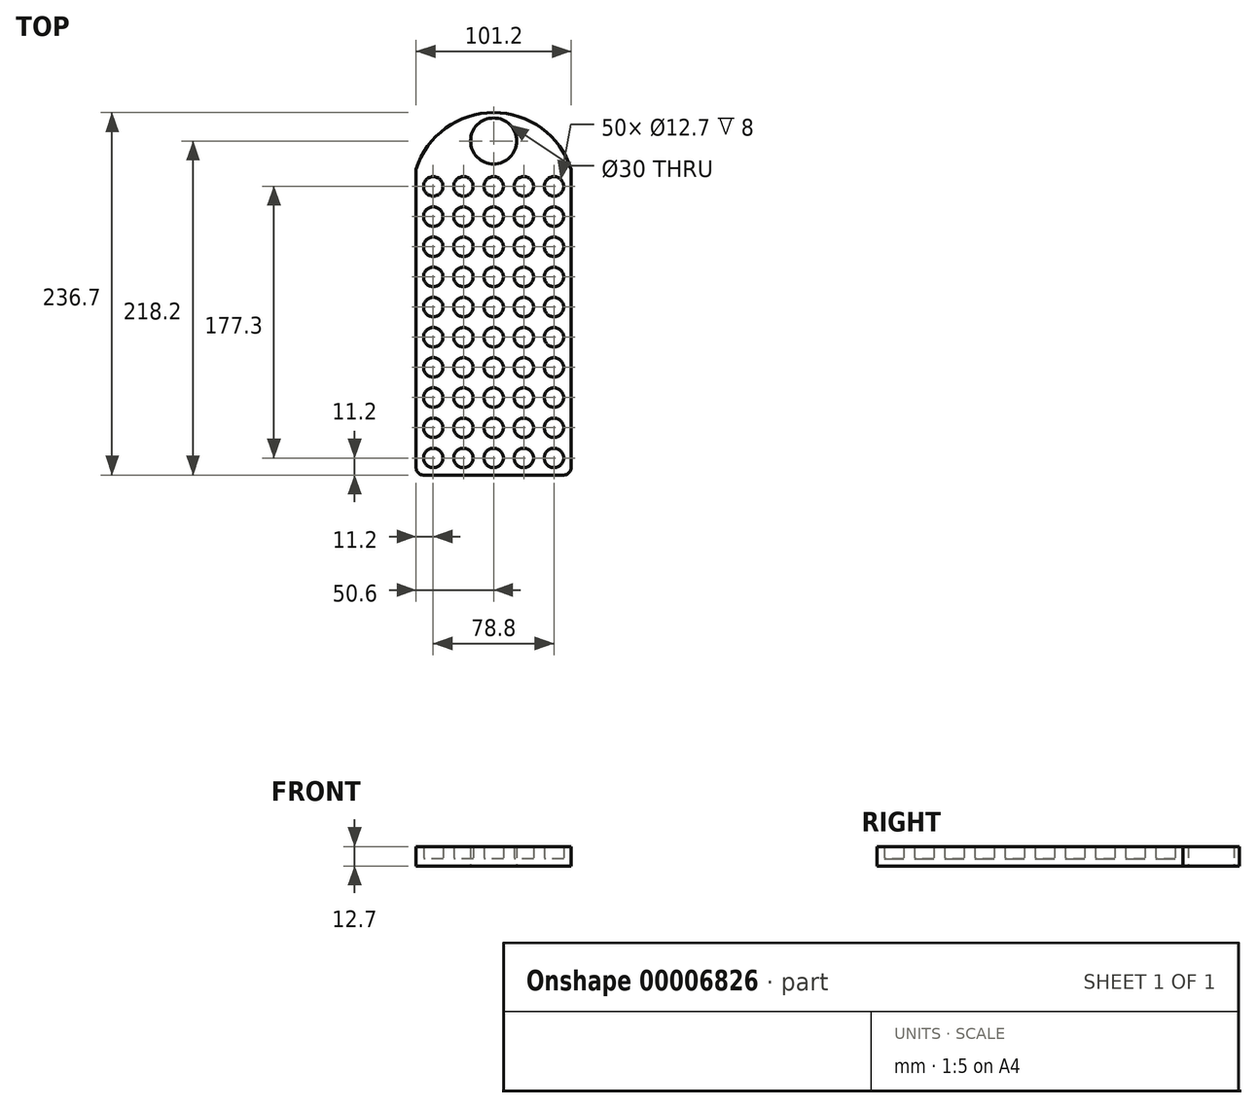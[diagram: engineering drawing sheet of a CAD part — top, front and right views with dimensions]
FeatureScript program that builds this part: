
annotation { "Feature Type Name" : "Feature", "Feature Type Description" : "" }
export const myFeature = defineFeature(function(context is Context, id is Id, definition is map)
    precondition{}
    {
        {
            var Q0;
            Q0=qCreatedBy(makeId("Top.planeOp"),FACE);
            var sketch = newSketch(context, id + "F0", { "sketchPlane" : qUnion([Q0])});
            skLineSegment(sketch, "E0", {"start": v(0, 0) * mm, "end": v(11.2, 0) * mm, "construction": true});
            skLineSegment(sketch, "E1", {"start": v(11.2, 0) * mm, "end": v(30.9, 0) * mm, "construction": true});
            skLineSegment(sketch, "E2", {"start": v(25.5, 0) * mm, "end": v(30.9, 0) * mm, "construction": true});
            skLineSegment(sketch, "E3", {"start": v(47.9, 0) * mm, "end": v(50.6, 0) * mm, "construction": true});
            skLineSegment(sketch, "E4", {"start": v(0, 0) * mm, "end": v(0, 11.2) * mm, "construction": true});
            skLineSegment(sketch, "E5", {"start": v(0, 11.2) * mm, "end": v(70.3, 11.2) * mm, "construction": true});
            skLineSegment(sketch, "E6", {"start": v(11.2, 0) * mm, "end": v(11.2, 11.2) * mm, "construction": true});
            skLineSegment(sketch, "E7", {"start": v(30.9, 0) * mm, "end": v(30.9, 11.2) * mm, "construction": true});
            skLineSegment(sketch, "E8", {"start": v(50.6, 0) * mm, "end": v(50.6, 11.2) * mm, "construction": true});
            skLineSegment(sketch, "E9", {"start": v(70.3, 0) * mm, "end": v(70.3, 11.2) * mm, "construction": true});
            skCircle(sketch, "E10", {"center": v(11.2, 11.2) * mm, "radius": 6.35 * mm});
            skLineSegment(sketch, "E11", {"start": v(70.3, 0) * mm, "end": v(90, 0) * mm, "construction": true});
            skLineSegment(sketch, "E12", {"start": v(70.3, 11.2) * mm, "end": v(90, 11.2) * mm, "construction": true});
            skLineSegment(sketch, "E13", {"start": v(90, 0) * mm, "end": v(90, 11.2) * mm, "construction": true});
            skCircle(sketch, "E14", {"center": v(30.9, 11.2) * mm, "radius": 6.35 * mm});
            skCircle(sketch, "E15", {"center": v(50.6, 11.2) * mm, "radius": 6.35 * mm});
            skCircle(sketch, "E16", {"center": v(70.3, 11.2) * mm, "radius": 6.35 * mm});
            skLineSegment(sketch, "E17", {"start": v(90, 0) * mm, "end": v(101.2, 0) * mm, "construction": true});
            skLineSegment(sketch, "E18", {"start": v(101.2, 11.2) * mm, "end": v(90, 11.2) * mm, "construction": true});
            skLineSegment(sketch, "E19", {"start": v(101.2, 0) * mm, "end": v(101.2, 11.2) * mm});
            skCircle(sketch, "E20", {"center": v(90, 11.2) * mm, "radius": 6.35 * mm});
            skLineSegment(sketch, "E21", {"start": v(0, 11.2) * mm, "end": v(0, 30.9) * mm, "construction": true});
            skLineSegment(sketch, "E22", {"start": v(0, 30.9) * mm, "end": v(101.2, 30.9) * mm, "construction": true});
            skLineSegment(sketch, "E23", {"start": v(11.2, 11.2) * mm, "end": v(11.2, 30.9) * mm, "construction": true});
            skLineSegment(sketch, "E24", {"start": v(30.9, 11.2) * mm, "end": v(30.9, 30.9) * mm, "construction": true});
            skLineSegment(sketch, "E25", {"start": v(50.6, 11.2) * mm, "end": v(50.6, 30.9) * mm, "construction": true});
            skLineSegment(sketch, "E26", {"start": v(70.3, 11.2) * mm, "end": v(70.3, 30.9) * mm, "construction": true});
            skLineSegment(sketch, "E27", {"start": v(90, 11.2) * mm, "end": v(90, 30.9) * mm, "construction": true});
            skLineSegment(sketch, "E28", {"start": v(101.2, 11.2) * mm, "end": v(101.2, 30.9) * mm, "construction": true});
            skCircle(sketch, "E29", {"center": v(11.2, 30.9) * mm, "radius": 6.35 * mm});
            skCircle(sketch, "E30", {"center": v(30.9, 30.9) * mm, "radius": 6.35 * mm});
            skCircle(sketch, "E31", {"center": v(50.6, 30.9) * mm, "radius": 6.35 * mm});
            skCircle(sketch, "E32", {"center": v(70.3, 30.9) * mm, "radius": 6.35 * mm});
            skCircle(sketch, "E33", {"center": v(90, 30.9) * mm, "radius": 6.35 * mm});
            skLineSegment(sketch, "E34", {"start": v(0, 30.9) * mm, "end": v(0, 50.6) * mm, "construction": true});
            skLineSegment(sketch, "E35", {"start": v(0, 50.6) * mm, "end": v(101.2, 50.6) * mm, "construction": true});
            skLineSegment(sketch, "E36", {"start": v(101.2, 30.9) * mm, "end": v(101.2, 50.6) * mm, "construction": true});
            skLineSegment(sketch, "E37", {"start": v(90, 30.9) * mm, "end": v(90, 50.6) * mm, "construction": true});
            skLineSegment(sketch, "E38", {"start": v(70.3, 30.9) * mm, "end": v(70.3, 50.6) * mm, "construction": true});
            skLineSegment(sketch, "E39", {"start": v(50.6, 30.9) * mm, "end": v(50.6, 50.6) * mm, "construction": true});
            skLineSegment(sketch, "E40", {"start": v(30.9, 30.9) * mm, "end": v(30.9, 50.6) * mm, "construction": true});
            skLineSegment(sketch, "E41", {"start": v(11.2, 30.9) * mm, "end": v(11.2, 50.6) * mm, "construction": true});
            skLineSegment(sketch, "E42", {"start": v(0, 50.6) * mm, "end": v(0, 70.3) * mm, "construction": true});
            skLineSegment(sketch, "E43", {"start": v(0, 70.3) * mm, "end": v(101.2, 70.3) * mm, "construction": true});
            skLineSegment(sketch, "E44", {"start": v(101.2, 50.6) * mm, "end": v(101.2, 70.3) * mm, "construction": true});
            skLineSegment(sketch, "E45", {"start": v(90, 50.6) * mm, "end": v(90, 70.3) * mm, "construction": true});
            skLineSegment(sketch, "E46", {"start": v(70.3, 50.6) * mm, "end": v(70.3, 70.3) * mm, "construction": true});
            skLineSegment(sketch, "E47", {"start": v(50.6, 50.6) * mm, "end": v(50.6, 70.3) * mm, "construction": true});
            skLineSegment(sketch, "E48", {"start": v(30.9, 50.6) * mm, "end": v(30.9, 70.3) * mm, "construction": true});
            skLineSegment(sketch, "E49", {"start": v(11.2, 50.6) * mm, "end": v(11.2, 70.3) * mm, "construction": true});
            skLineSegment(sketch, "E50", {"start": v(0, 70.3) * mm, "end": v(0, 90) * mm, "construction": true});
            skLineSegment(sketch, "E51", {"start": v(0, 90) * mm, "end": v(84.97, 90) * mm, "construction": true});
            skLineSegment(sketch, "E52", {"start": v(11.2, 70.3) * mm, "end": v(11.2, 90) * mm, "construction": true});
            skLineSegment(sketch, "E53", {"start": v(30.9, 70.3) * mm, "end": v(30.9, 90) * mm, "construction": true});
            skLineSegment(sketch, "E54", {"start": v(50.6, 70.3) * mm, "end": v(50.6, 90) * mm, "construction": true});
            skLineSegment(sketch, "E55", {"start": v(70.3, 70.3) * mm, "end": v(70.3, 90) * mm, "construction": true});
            skLineSegment(sketch, "E56", {"start": v(90, 70.3) * mm, "end": v(90, 90) * mm, "construction": true});
            skLineSegment(sketch, "E57", {"start": v(101.2, 70.3) * mm, "end": v(101.2, 90) * mm, "construction": true});
            skCircle(sketch, "E58", {"center": v(11.2, 50.6) * mm, "radius": 6.35 * mm});
            skCircle(sketch, "E59", {"center": v(11.2, 70.3) * mm, "radius": 6.35 * mm});
            skCircle(sketch, "E60", {"center": v(11.2, 90) * mm, "radius": 6.35 * mm});
            skCircle(sketch, "E61", {"center": v(30.9, 90) * mm, "radius": 6.35 * mm});
            skCircle(sketch, "E62", {"center": v(30.9, 70.3) * mm, "radius": 6.35 * mm});
            skCircle(sketch, "E63", {"center": v(30.9, 50.6) * mm, "radius": 6.35 * mm});
            skCircle(sketch, "E64", {"center": v(50.6, 90) * mm, "radius": 6.35 * mm});
            skCircle(sketch, "E65", {"center": v(50.6, 70.3) * mm, "radius": 6.35 * mm});
            skCircle(sketch, "E66", {"center": v(50.6, 50.6) * mm, "radius": 6.35 * mm});
            skCircle(sketch, "E67", {"center": v(70.3, 50.6) * mm, "radius": 6.35 * mm});
            skCircle(sketch, "E68", {"center": v(70.3, 70.3) * mm, "radius": 6.35 * mm});
            skCircle(sketch, "E69", {"center": v(70.3, 90) * mm, "radius": 6.35 * mm});
            skCircle(sketch, "E70", {"center": v(90, 90) * mm, "radius": 6.35 * mm});
            skCircle(sketch, "E71", {"center": v(90, 70.3) * mm, "radius": 6.35 * mm});
            skCircle(sketch, "E72", {"center": v(90, 50.6) * mm, "radius": 6.35 * mm});
            skLineSegment(sketch, "E73", {"start": v(0, 90) * mm, "end": v(0, 109.7) * mm, "construction": true});
            skLineSegment(sketch, "E74", {"start": v(0, 109.7) * mm, "end": v(101.2, 109.7) * mm, "construction": true});
            skLineSegment(sketch, "E75", {"start": v(11.2, 90) * mm, "end": v(11.2, 109.7) * mm, "construction": true});
            skLineSegment(sketch, "E76", {"start": v(30.9, 90) * mm, "end": v(30.9, 109.7) * mm, "construction": true});
            skLineSegment(sketch, "E77", {"start": v(50.6, 90) * mm, "end": v(50.6, 109.7) * mm, "construction": true});
            skLineSegment(sketch, "E78", {"start": v(70.3, 90) * mm, "end": v(70.3, 109.7) * mm, "construction": true});
            skLineSegment(sketch, "E79", {"start": v(89.88, 87.08) * mm, "end": v(90, 109.7) * mm, "construction": true});
            skLineSegment(sketch, "E80", {"start": v(90, 109.7) * mm, "end": v(90, 109.7) * mm});
            skLineSegment(sketch, "E81", {"start": v(101.2, 90) * mm, "end": v(101.2, 109.7) * mm, "construction": true});
            skLineSegment(sketch, "E82", {"start": v(0, 109.7) * mm, "end": v(0, 129.4) * mm, "construction": true});
            skLineSegment(sketch, "E83", {"start": v(0, 129.4) * mm, "end": v(101.2, 129.4) * mm, "construction": true});
            skLineSegment(sketch, "E84", {"start": v(11.2, 109.7) * mm, "end": v(11.2, 129.4) * mm, "construction": true});
            skLineSegment(sketch, "E85", {"start": v(30.9, 109.7) * mm, "end": v(30.9, 129.4) * mm, "construction": true});
            skLineSegment(sketch, "E86", {"start": v(50.6, 109.7) * mm, "end": v(50.6, 129.4) * mm, "construction": true});
            skLineSegment(sketch, "E87", {"start": v(70.3, 109.7) * mm, "end": v(70.3, 129.4) * mm, "construction": true});
            skLineSegment(sketch, "E88", {"start": v(90, 109.7) * mm, "end": v(90, 129.4) * mm, "construction": true});
            skLineSegment(sketch, "E89", {"start": v(101.2, 109.7) * mm, "end": v(101.2, 129.4) * mm, "construction": true});
            skLineSegment(sketch, "E90", {"start": v(0, 129.4) * mm, "end": v(0, 149.1) * mm, "construction": true});
            skLineSegment(sketch, "E91", {"start": v(0, 149.1) * mm, "end": v(101.2, 149.1) * mm, "construction": true});
            skLineSegment(sketch, "E92", {"start": v(11.2, 129.4) * mm, "end": v(11.2, 149.1) * mm, "construction": true});
            skLineSegment(sketch, "E93", {"start": v(30.9, 129.4) * mm, "end": v(30.9, 149.1) * mm, "construction": true});
            skLineSegment(sketch, "E94", {"start": v(50.6, 129.4) * mm, "end": v(50.6, 149.1) * mm, "construction": true});
            skLineSegment(sketch, "E95", {"start": v(70.3, 129.4) * mm, "end": v(70.3, 149.1) * mm, "construction": true});
            skLineSegment(sketch, "E96", {"start": v(90, 129.4) * mm, "end": v(90, 149.1) * mm, "construction": true});
            skLineSegment(sketch, "E97", {"start": v(101.2, 129.4) * mm, "end": v(101.2, 149.1) * mm, "construction": true});
            skLineSegment(sketch, "E98", {"start": v(0, 149.1) * mm, "end": v(0, 168.8) * mm, "construction": true});
            skLineSegment(sketch, "E99", {"start": v(0, 168.8) * mm, "end": v(101.2, 168.8) * mm, "construction": true});
            skLineSegment(sketch, "E100", {"start": v(11.2, 149.1) * mm, "end": v(11.2, 168.8) * mm, "construction": true});
            skLineSegment(sketch, "E101", {"start": v(30.9, 149.1) * mm, "end": v(30.9, 168.8) * mm, "construction": true});
            skLineSegment(sketch, "E102", {"start": v(50.6, 149.1) * mm, "end": v(50.6, 168.8) * mm, "construction": true});
            skLineSegment(sketch, "E103", {"start": v(70.3, 149.1) * mm, "end": v(70.3, 168.8) * mm, "construction": true});
            skLineSegment(sketch, "E104", {"start": v(90, 149.1) * mm, "end": v(90, 168.8) * mm, "construction": true});
            skLineSegment(sketch, "E105", {"start": v(101.2, 149.1) * mm, "end": v(101.2, 168.8) * mm, "construction": true});
            skLineSegment(sketch, "E106", {"start": v(0, 168.8) * mm, "end": v(0, 188.5) * mm, "construction": true});
            skLineSegment(sketch, "E107", {"start": v(0, 188.5) * mm, "end": v(101.2, 188.5) * mm, "construction": true});
            skLineSegment(sketch, "E108", {"start": v(11.2, 168.8) * mm, "end": v(11.2, 188.5) * mm, "construction": true});
            skLineSegment(sketch, "E109", {"start": v(30.9, 168.8) * mm, "end": v(30.9, 188.5) * mm, "construction": true});
            skLineSegment(sketch, "E110", {"start": v(50.6, 168.8) * mm, "end": v(50.6, 188.5) * mm, "construction": true});
            skLineSegment(sketch, "E111", {"start": v(70.3, 168.8) * mm, "end": v(70.3, 188.5) * mm, "construction": true});
            skLineSegment(sketch, "E112", {"start": v(90, 168.8) * mm, "end": v(90, 188.5) * mm, "construction": true});
            skLineSegment(sketch, "E113", {"start": v(101.2, 168.8) * mm, "end": v(101.2, 188.5) * mm, "construction": true});
            skCircle(sketch, "E114", {"center": v(11.2, 188.5) * mm, "radius": 6.35 * mm});
            skCircle(sketch, "E115", {"center": v(11.2, 168.8) * mm, "radius": 6.35 * mm});
            skCircle(sketch, "E116", {"center": v(11.2, 149.1) * mm, "radius": 6.35 * mm});
            skCircle(sketch, "E117", {"center": v(11.2, 129.4) * mm, "radius": 6.35 * mm});
            skCircle(sketch, "E118", {"center": v(11.2, 109.7) * mm, "radius": 6.35 * mm});
            skCircle(sketch, "E119", {"center": v(30.9, 109.7) * mm, "radius": 6.35 * mm});
            skCircle(sketch, "E120", {"center": v(30.9, 129.4) * mm, "radius": 6.35 * mm});
            skCircle(sketch, "E121", {"center": v(30.9, 149.1) * mm, "radius": 6.35 * mm});
            skCircle(sketch, "E122", {"center": v(30.9, 168.8) * mm, "radius": 6.35 * mm});
            skCircle(sketch, "E123", {"center": v(30.9, 188.5) * mm, "radius": 6.35 * mm});
            skCircle(sketch, "E124", {"center": v(50.6, 188.5) * mm, "radius": 6.35 * mm});
            skCircle(sketch, "E125", {"center": v(50.6, 168.8) * mm, "radius": 6.35 * mm});
            skCircle(sketch, "E126", {"center": v(50.6, 149.1) * mm, "radius": 6.35 * mm});
            skCircle(sketch, "E127", {"center": v(50.6, 129.4) * mm, "radius": 6.35 * mm});
            skCircle(sketch, "E128", {"center": v(50.6, 109.7) * mm, "radius": 6.35 * mm});
            skCircle(sketch, "E129", {"center": v(90, 109.7) * mm, "radius": 6.35 * mm});
            skCircle(sketch, "E130", {"center": v(70.3, 109.7) * mm, "radius": 6.35 * mm});
            skCircle(sketch, "E131", {"center": v(70.3, 129.4) * mm, "radius": 6.35 * mm});
            skCircle(sketch, "E132", {"center": v(90, 129.4) * mm, "radius": 6.35 * mm});
            skCircle(sketch, "E133", {"center": v(90, 149.1) * mm, "radius": 6.35 * mm});
            skCircle(sketch, "E134", {"center": v(70.3, 149.1) * mm, "radius": 6.35 * mm});
            skCircle(sketch, "E135", {"center": v(70.3, 168.8) * mm, "radius": 6.35 * mm});
            skCircle(sketch, "E136", {"center": v(90, 168.8) * mm, "radius": 6.35 * mm});
            skCircle(sketch, "E137", {"center": v(70.3, 188.5) * mm, "radius": 6.35 * mm});
            skCircle(sketch, "E138", {"center": v(90, 188.5) * mm, "radius": 6.35 * mm});
            skLineSegment(sketch, "E139", {"start": v(101.2, 188.5) * mm, "end": v(101.2, 199.7) * mm, "construction": true});
            skLineSegment(sketch, "E140", {"start": v(30.9, 0) * mm, "end": v(50.6, 0) * mm, "construction": true});
            skLineSegment(sketch, "E141", {"start": v(50.6, 0) * mm, "end": v(70.3, 0) * mm, "construction": true});
            skSolve(sketch);
        }
        {
            var Q0;
            Q0=qCreatedBy(makeId("Top.planeOp"),FACE);
            var sketch = newSketch(context, id + "F1", { "sketchPlane" : qUnion([Q0])});
            skLineSegment(sketch, "E142.bottom", {"start": v(5, 0) * mm, "end": v(96.2, 0) * mm});
            skLineSegment(sketch, "E142.top", {"start": v(0, 199.7) * mm, "end": v(101.2, 199.7) * mm, "construction": true});
            skLineSegment(sketch, "E142.left", {"start": v(0, 5) * mm, "end": v(0, 199.7) * mm});
            skLineSegment(sketch, "E142.right", {"start": v(101.2, 5) * mm, "end": v(101.2, 199.7) * mm});
            skPoint(sketch, "E143.visualSharp", {"position": v(101.2, 0) * mm});
            skArc(sketch, "E143.filletArc", {"start": v(96.2, 0) * mm, "mid": v(99.74, 1.46) * mm, "end": v(101.2, 5) * mm});
            skPoint(sketch, "E144.visualSharp", {"position": v(0, 0) * mm});
            skArc(sketch, "E144.filletArc", {"start": v(0, 5) * mm, "mid": v(1.46, 1.46) * mm, "end": v(5, 0) * mm});
            skLineSegment(sketch, "E145", {"start": v(50.6, 199.7) * mm, "end": v(50.6, 218.2) * mm, "construction": true});
            skCircle(sketch, "E146", {"center": v(50.6, 218.2) * mm, "radius": 15 * mm});
            skLineSegment(sketch, "E147", {"start": v(50.6, 218.2) * mm, "end": v(50.6, 233.2) * mm, "construction": true});
            skLineSegment(sketch, "E148", {"start": v(50.6, 233.2) * mm, "end": v(50.6, 236.7) * mm, "construction": true});
            skLineSegment(sketch, "E149", {"start": v(50.6, 199.7) * mm, "end": v(50.6, 203.2) * mm, "construction": true});
            skArc(sketch, "E150", {"start": v(101.2, 199.7) * mm, "mid": v(50.6, 236.7) * mm, "end": v(0, 199.7) * mm});
            skSolve(sketch);
        }
        {
            var Q0;
            Q0=qSketchRegion(id+"F0",true);
            extrude(context, id + "F2", {"entities" : qUnion([Q0]), "depth" : 4.7 * mm});
        }
        {
            var Q0;
            Q0=makeQuery(id+"F2.opExtrude","CAP_FACE",FACE,{"disambiguationData":[OSD([sQuery(id+"F0.wireOp",EDGE,"E15")])],"isStart":false});
            var Q1;
            Q1=makeQuery(id+"F2.opExtrude","CAP_FACE",FACE,{"disambiguationData":[OSD([sQuery(id+"F0.wireOp",EDGE,"E16")])],"isStart":false});
            var Q2;
            Q2=makeQuery(id+"F2.opExtrude","CAP_FACE",FACE,{"disambiguationData":[OSD([sQuery(id+"F0.wireOp",EDGE,"E20")])],"isStart":false});
            var Q3;
            Q3=makeQuery(id+"F2.opExtrude","CAP_FACE",FACE,{"disambiguationData":[OSD([sQuery(id+"F0.wireOp",EDGE,"E33")])],"isStart":false});
            var Q4;
            Q4=makeQuery(id+"F2.opExtrude","CAP_FACE",FACE,{"disambiguationData":[OSD([sQuery(id+"F0.wireOp",EDGE,"E32")])],"isStart":false});
            var Q5;
            Q5=makeQuery(id+"F2.opExtrude","CAP_FACE",FACE,{"disambiguationData":[OSD([sQuery(id+"F0.wireOp",EDGE,"E31")])],"isStart":false});
            var Q6;
            Q6=makeQuery(id+"F2.opExtrude","CAP_FACE",FACE,{"disambiguationData":[OSD([sQuery(id+"F0.wireOp",EDGE,"E30")])],"isStart":false});
            var Q7;
            Q7=makeQuery(id+"F2.opExtrude","CAP_FACE",FACE,{"disambiguationData":[OSD([sQuery(id+"F0.wireOp",EDGE,"E14")])],"isStart":false});
            var Q8;
            Q8=makeQuery(id+"F2.opExtrude","CAP_FACE",FACE,{"disambiguationData":[OSD([sQuery(id+"F0.wireOp",EDGE,"E10")])],"isStart":false});
            var Q9;
            Q9=makeQuery(id+"F2.opExtrude","CAP_FACE",FACE,{"disambiguationData":[OSD([sQuery(id+"F0.wireOp",EDGE,"E29")])],"isStart":false});
            var Q10;
            Q10=makeQuery(id+"F2.opExtrude","CAP_FACE",FACE,{"disambiguationData":[OSD([sQuery(id+"F0.wireOp",EDGE,"E58")])],"isStart":false});
            var Q11;
            Q11=makeQuery(id+"F2.opExtrude","CAP_FACE",FACE,{"disambiguationData":[OSD([sQuery(id+"F0.wireOp",EDGE,"E63")])],"isStart":false});
            var Q12;
            Q12=makeQuery(id+"F2.opExtrude","CAP_FACE",FACE,{"disambiguationData":[OSD([sQuery(id+"F0.wireOp",EDGE,"E66")])],"isStart":false});
            var Q13;
            Q13=makeQuery(id+"F2.opExtrude","CAP_FACE",FACE,{"disambiguationData":[OSD([sQuery(id+"F0.wireOp",EDGE,"E67")])],"isStart":false});
            var Q14;
            Q14=makeQuery(id+"F2.opExtrude","CAP_FACE",FACE,{"disambiguationData":[OSD([sQuery(id+"F0.wireOp",EDGE,"E72")])],"isStart":false});
            var Q15;
            Q15=makeQuery(id+"F2.opExtrude","CAP_FACE",FACE,{"disambiguationData":[OSD([sQuery(id+"F0.wireOp",EDGE,"E71")])],"isStart":false});
            var Q16;
            Q16=makeQuery(id+"F2.opExtrude","CAP_FACE",FACE,{"disambiguationData":[OSD([sQuery(id+"F0.wireOp",EDGE,"E68")])],"isStart":false});
            var Q17;
            Q17=makeQuery(id+"F2.opExtrude","CAP_FACE",FACE,{"disambiguationData":[OSD([sQuery(id+"F0.wireOp",EDGE,"E65")])],"isStart":false});
            var Q18;
            Q18=makeQuery(id+"F2.opExtrude","CAP_FACE",FACE,{"disambiguationData":[OSD([sQuery(id+"F0.wireOp",EDGE,"E62")])],"isStart":false});
            var Q19;
            Q19=makeQuery(id+"F2.opExtrude","CAP_FACE",FACE,{"disambiguationData":[OSD([sQuery(id+"F0.wireOp",EDGE,"E59")])],"isStart":false});
            var Q20;
            Q20=makeQuery(id+"F2.opExtrude","CAP_FACE",FACE,{"disambiguationData":[OSD([sQuery(id+"F0.wireOp",EDGE,"E60")])],"isStart":false});
            var Q21;
            Q21=makeQuery(id+"F2.opExtrude","CAP_FACE",FACE,{"disambiguationData":[OSD([sQuery(id+"F0.wireOp",EDGE,"E118")])],"isStart":false});
            var Q22;
            Q22=makeQuery(id+"F2.opExtrude","CAP_FACE",FACE,{"disambiguationData":[OSD([sQuery(id+"F0.wireOp",EDGE,"E117")])],"isStart":false});
            var Q23;
            Q23=makeQuery(id+"F2.opExtrude","CAP_FACE",FACE,{"disambiguationData":[OSD([sQuery(id+"F0.wireOp",EDGE,"E116")])],"isStart":false});
            var Q24;
            Q24=makeQuery(id+"F2.opExtrude","CAP_FACE",FACE,{"disambiguationData":[OSD([sQuery(id+"F0.wireOp",EDGE,"E115")])],"isStart":false});
            var Q25;
            Q25=makeQuery(id+"F2.opExtrude","CAP_FACE",FACE,{"disambiguationData":[OSD([sQuery(id+"F0.wireOp",EDGE,"E114")])],"isStart":false});
            var Q26;
            Q26=makeQuery(id+"F2.opExtrude","CAP_FACE",FACE,{"disambiguationData":[OSD([sQuery(id+"F0.wireOp",EDGE,"E123")])],"isStart":false});
            var Q27;
            Q27=makeQuery(id+"F2.opExtrude","CAP_FACE",FACE,{"disambiguationData":[OSD([sQuery(id+"F0.wireOp",EDGE,"E122")])],"isStart":false});
            var Q28;
            Q28=makeQuery(id+"F2.opExtrude","CAP_FACE",FACE,{"disambiguationData":[OSD([sQuery(id+"F0.wireOp",EDGE,"E121")])],"isStart":false});
            var Q29;
            Q29=makeQuery(id+"F2.opExtrude","CAP_FACE",FACE,{"disambiguationData":[OSD([sQuery(id+"F0.wireOp",EDGE,"E120")])],"isStart":false});
            var Q30;
            Q30=makeQuery(id+"F2.opExtrude","CAP_FACE",FACE,{"disambiguationData":[OSD([sQuery(id+"F0.wireOp",EDGE,"E119")])],"isStart":false});
            var Q31;
            Q31=makeQuery(id+"F2.opExtrude","CAP_FACE",FACE,{"disambiguationData":[OSD([sQuery(id+"F0.wireOp",EDGE,"E61")])],"isStart":false});
            var Q32;
            Q32=makeQuery(id+"F2.opExtrude","CAP_FACE",FACE,{"disambiguationData":[OSD([sQuery(id+"F0.wireOp",EDGE,"E64")])],"isStart":false});
            var Q33;
            Q33=makeQuery(id+"F2.opExtrude","CAP_FACE",FACE,{"disambiguationData":[OSD([sQuery(id+"F0.wireOp",EDGE,"E69")])],"isStart":false});
            var Q34;
            Q34=makeQuery(id+"F2.opExtrude","CAP_FACE",FACE,{"disambiguationData":[OSD([sQuery(id+"F0.wireOp",EDGE,"E70")])],"isStart":false});
            var Q35;
            Q35=makeQuery(id+"F2.opExtrude","CAP_FACE",FACE,{"disambiguationData":[OSD([sQuery(id+"F0.wireOp",EDGE,"E129")])],"isStart":false});
            var Q36;
            Q36=makeQuery(id+"F2.opExtrude","CAP_FACE",FACE,{"disambiguationData":[OSD([sQuery(id+"F0.wireOp",EDGE,"E130")])],"isStart":false});
            var Q37;
            Q37=makeQuery(id+"F2.opExtrude","CAP_FACE",FACE,{"disambiguationData":[OSD([sQuery(id+"F0.wireOp",EDGE,"E128")])],"isStart":false});
            var Q38;
            Q38=makeQuery(id+"F2.opExtrude","CAP_FACE",FACE,{"disambiguationData":[OSD([sQuery(id+"F0.wireOp",EDGE,"E127")])],"isStart":false});
            var Q39;
            Q39=makeQuery(id+"F2.opExtrude","CAP_FACE",FACE,{"disambiguationData":[OSD([sQuery(id+"F0.wireOp",EDGE,"E131")])],"isStart":false});
            var Q40;
            Q40=makeQuery(id+"F2.opExtrude","CAP_FACE",FACE,{"disambiguationData":[OSD([sQuery(id+"F0.wireOp",EDGE,"E132")])],"isStart":false});
            var Q41;
            Q41=makeQuery(id+"F2.opExtrude","CAP_FACE",FACE,{"disambiguationData":[OSD([sQuery(id+"F0.wireOp",EDGE,"E133")])],"isStart":false});
            var Q42;
            Q42=makeQuery(id+"F2.opExtrude","CAP_FACE",FACE,{"disambiguationData":[OSD([sQuery(id+"F0.wireOp",EDGE,"E134")])],"isStart":false});
            var Q43;
            Q43=makeQuery(id+"F2.opExtrude","CAP_FACE",FACE,{"disambiguationData":[OSD([sQuery(id+"F0.wireOp",EDGE,"E126")])],"isStart":false});
            var Q44;
            Q44=makeQuery(id+"F2.opExtrude","CAP_FACE",FACE,{"disambiguationData":[OSD([sQuery(id+"F0.wireOp",EDGE,"E125")])],"isStart":false});
            var Q45;
            Q45=makeQuery(id+"F2.opExtrude","CAP_FACE",FACE,{"disambiguationData":[OSD([sQuery(id+"F0.wireOp",EDGE,"E124")])],"isStart":false});
            var Q46;
            Q46=makeQuery(id+"F2.opExtrude","CAP_FACE",FACE,{"disambiguationData":[OSD([sQuery(id+"F0.wireOp",EDGE,"E137")])],"isStart":false});
            var Q47;
            Q47=makeQuery(id+"F2.opExtrude","CAP_FACE",FACE,{"disambiguationData":[OSD([sQuery(id+"F0.wireOp",EDGE,"E135")])],"isStart":false});
            var Q48;
            Q48=makeQuery(id+"F2.opExtrude","CAP_FACE",FACE,{"disambiguationData":[OSD([sQuery(id+"F0.wireOp",EDGE,"E136")])],"isStart":false});
            var Q49;
            Q49=makeQuery(id+"F2.opExtrude","CAP_FACE",FACE,{"disambiguationData":[OSD([sQuery(id+"F0.wireOp",EDGE,"E138")])],"isStart":false});
            extrude(context, id + "F3", {"entities" : qUnion([Q0, Q1, Q2, Q3, Q4, Q5, Q6, Q7, Q8, Q9, Q10, Q11, Q12, Q13, Q14, Q15, Q16, Q17, Q18, Q19, Q20, Q21, Q22, Q23, Q24, Q25, Q26, Q27, Q28, Q29, Q30, Q31, Q32, Q33, Q34, Q35, Q36, Q37, Q38, Q39, Q40, Q41, Q42, Q43, Q44, Q45, Q46, Q47, Q48, Q49]), "depth" : 8 * mm});
        }
        {
            var Q0;
            Q0=makeQuery(id+"F2.opExtrude","SWEPT_BODY",BODY,{"disambiguationData":[OSD([sQuery(id+"F0.wireOp",EDGE,"E10")])]});
            var Q1;
            Q1=makeQuery(id+"F2.opExtrude","SWEPT_BODY",BODY,{"disambiguationData":[OSD([sQuery(id+"F0.wireOp",EDGE,"E14")])]});
            var Q2;
            Q2=makeQuery(id+"F2.opExtrude","SWEPT_BODY",BODY,{"disambiguationData":[OSD([sQuery(id+"F0.wireOp",EDGE,"E15")])]});
            var Q3;
            Q3=makeQuery(id+"F2.opExtrude","SWEPT_BODY",BODY,{"disambiguationData":[OSD([sQuery(id+"F0.wireOp",EDGE,"E16")])]});
            var Q4;
            Q4=makeQuery(id+"F2.opExtrude","SWEPT_BODY",BODY,{"disambiguationData":[OSD([sQuery(id+"F0.wireOp",EDGE,"E20")])]});
            var Q5;
            Q5=makeQuery(id+"F2.opExtrude","SWEPT_BODY",BODY,{"disambiguationData":[OSD([sQuery(id+"F0.wireOp",EDGE,"E29")])]});
            var Q6;
            Q6=makeQuery(id+"F2.opExtrude","SWEPT_BODY",BODY,{"disambiguationData":[OSD([sQuery(id+"F0.wireOp",EDGE,"E30")])]});
            var Q7;
            Q7=makeQuery(id+"F2.opExtrude","SWEPT_BODY",BODY,{"disambiguationData":[OSD([sQuery(id+"F0.wireOp",EDGE,"E31")])]});
            var Q8;
            Q8=makeQuery(id+"F2.opExtrude","SWEPT_BODY",BODY,{"disambiguationData":[OSD([sQuery(id+"F0.wireOp",EDGE,"E32")])]});
            var Q9;
            Q9=makeQuery(id+"F2.opExtrude","SWEPT_BODY",BODY,{"disambiguationData":[OSD([sQuery(id+"F0.wireOp",EDGE,"E33")])]});
            var Q10;
            Q10=makeQuery(id+"F2.opExtrude","SWEPT_BODY",BODY,{"disambiguationData":[OSD([sQuery(id+"F0.wireOp",EDGE,"E58")])]});
            var Q11;
            Q11=makeQuery(id+"F2.opExtrude","SWEPT_BODY",BODY,{"disambiguationData":[OSD([sQuery(id+"F0.wireOp",EDGE,"E59")])]});
            var Q12;
            Q12=makeQuery(id+"F2.opExtrude","SWEPT_BODY",BODY,{"disambiguationData":[OSD([sQuery(id+"F0.wireOp",EDGE,"E60")])]});
            var Q13;
            Q13=makeQuery(id+"F2.opExtrude","SWEPT_BODY",BODY,{"disambiguationData":[OSD([sQuery(id+"F0.wireOp",EDGE,"E61")])]});
            var Q14;
            Q14=makeQuery(id+"F2.opExtrude","SWEPT_BODY",BODY,{"disambiguationData":[OSD([sQuery(id+"F0.wireOp",EDGE,"E62")])]});
            var Q15;
            Q15=makeQuery(id+"F2.opExtrude","SWEPT_BODY",BODY,{"disambiguationData":[OSD([sQuery(id+"F0.wireOp",EDGE,"E63")])]});
            var Q16;
            Q16=makeQuery(id+"F2.opExtrude","SWEPT_BODY",BODY,{"disambiguationData":[OSD([sQuery(id+"F0.wireOp",EDGE,"E64")])]});
            var Q17;
            Q17=makeQuery(id+"F2.opExtrude","SWEPT_BODY",BODY,{"disambiguationData":[OSD([sQuery(id+"F0.wireOp",EDGE,"E65")])]});
            var Q18;
            Q18=makeQuery(id+"F2.opExtrude","SWEPT_BODY",BODY,{"disambiguationData":[OSD([sQuery(id+"F0.wireOp",EDGE,"E66")])]});
            var Q19;
            Q19=makeQuery(id+"F2.opExtrude","SWEPT_BODY",BODY,{"disambiguationData":[OSD([sQuery(id+"F0.wireOp",EDGE,"E67")])]});
            var Q20;
            Q20=makeQuery(id+"F2.opExtrude","SWEPT_BODY",BODY,{"disambiguationData":[OSD([sQuery(id+"F0.wireOp",EDGE,"E68")])]});
            var Q21;
            Q21=makeQuery(id+"F2.opExtrude","SWEPT_BODY",BODY,{"disambiguationData":[OSD([sQuery(id+"F0.wireOp",EDGE,"E69")])]});
            var Q22;
            Q22=makeQuery(id+"F2.opExtrude","SWEPT_BODY",BODY,{"disambiguationData":[OSD([sQuery(id+"F0.wireOp",EDGE,"E70")])]});
            var Q23;
            Q23=makeQuery(id+"F2.opExtrude","SWEPT_BODY",BODY,{"disambiguationData":[OSD([sQuery(id+"F0.wireOp",EDGE,"E71")])]});
            var Q24;
            Q24=makeQuery(id+"F2.opExtrude","SWEPT_BODY",BODY,{"disambiguationData":[OSD([sQuery(id+"F0.wireOp",EDGE,"E72")])]});
            var Q25;
            Q25=makeQuery(id+"F2.opExtrude","SWEPT_BODY",BODY,{"disambiguationData":[OSD([sQuery(id+"F0.wireOp",EDGE,"E114")])]});
            var Q26;
            Q26=makeQuery(id+"F2.opExtrude","SWEPT_BODY",BODY,{"disambiguationData":[OSD([sQuery(id+"F0.wireOp",EDGE,"E115")])]});
            var Q27;
            Q27=makeQuery(id+"F2.opExtrude","SWEPT_BODY",BODY,{"disambiguationData":[OSD([sQuery(id+"F0.wireOp",EDGE,"E116")])]});
            var Q28;
            Q28=makeQuery(id+"F2.opExtrude","SWEPT_BODY",BODY,{"disambiguationData":[OSD([sQuery(id+"F0.wireOp",EDGE,"E117")])]});
            var Q29;
            Q29=makeQuery(id+"F2.opExtrude","SWEPT_BODY",BODY,{"disambiguationData":[OSD([sQuery(id+"F0.wireOp",EDGE,"E118")])]});
            var Q30;
            Q30=makeQuery(id+"F2.opExtrude","SWEPT_BODY",BODY,{"disambiguationData":[OSD([sQuery(id+"F0.wireOp",EDGE,"E119")])]});
            var Q31;
            Q31=makeQuery(id+"F2.opExtrude","SWEPT_BODY",BODY,{"disambiguationData":[OSD([sQuery(id+"F0.wireOp",EDGE,"E120")])]});
            var Q32;
            Q32=makeQuery(id+"F2.opExtrude","SWEPT_BODY",BODY,{"disambiguationData":[OSD([sQuery(id+"F0.wireOp",EDGE,"E121")])]});
            var Q33;
            Q33=makeQuery(id+"F2.opExtrude","SWEPT_BODY",BODY,{"disambiguationData":[OSD([sQuery(id+"F0.wireOp",EDGE,"E122")])]});
            var Q34;
            Q34=makeQuery(id+"F2.opExtrude","SWEPT_BODY",BODY,{"disambiguationData":[OSD([sQuery(id+"F0.wireOp",EDGE,"E123")])]});
            var Q35;
            Q35=makeQuery(id+"F2.opExtrude","SWEPT_BODY",BODY,{"disambiguationData":[OSD([sQuery(id+"F0.wireOp",EDGE,"E124")])]});
            var Q36;
            Q36=makeQuery(id+"F2.opExtrude","SWEPT_BODY",BODY,{"disambiguationData":[OSD([sQuery(id+"F0.wireOp",EDGE,"E125")])]});
            var Q37;
            Q37=makeQuery(id+"F2.opExtrude","SWEPT_BODY",BODY,{"disambiguationData":[OSD([sQuery(id+"F0.wireOp",EDGE,"E126")])]});
            var Q38;
            Q38=makeQuery(id+"F2.opExtrude","SWEPT_BODY",BODY,{"disambiguationData":[OSD([sQuery(id+"F0.wireOp",EDGE,"E127")])]});
            var Q39;
            Q39=makeQuery(id+"F2.opExtrude","SWEPT_BODY",BODY,{"disambiguationData":[OSD([sQuery(id+"F0.wireOp",EDGE,"E128")])]});
            var Q40;
            Q40=makeQuery(id+"F2.opExtrude","SWEPT_BODY",BODY,{"disambiguationData":[OSD([sQuery(id+"F0.wireOp",EDGE,"E129")])]});
            var Q41;
            Q41=makeQuery(id+"F2.opExtrude","SWEPT_BODY",BODY,{"disambiguationData":[OSD([sQuery(id+"F0.wireOp",EDGE,"E130")])]});
            var Q42;
            Q42=makeQuery(id+"F2.opExtrude","SWEPT_BODY",BODY,{"disambiguationData":[OSD([sQuery(id+"F0.wireOp",EDGE,"E131")])]});
            var Q43;
            Q43=makeQuery(id+"F2.opExtrude","SWEPT_BODY",BODY,{"disambiguationData":[OSD([sQuery(id+"F0.wireOp",EDGE,"E132")])]});
            var Q44;
            Q44=makeQuery(id+"F2.opExtrude","SWEPT_BODY",BODY,{"disambiguationData":[OSD([sQuery(id+"F0.wireOp",EDGE,"E133")])]});
            var Q45;
            Q45=makeQuery(id+"F2.opExtrude","SWEPT_BODY",BODY,{"disambiguationData":[OSD([sQuery(id+"F0.wireOp",EDGE,"E134")])]});
            var Q46;
            Q46=makeQuery(id+"F2.opExtrude","SWEPT_BODY",BODY,{"disambiguationData":[OSD([sQuery(id+"F0.wireOp",EDGE,"E135")])]});
            var Q47;
            Q47=makeQuery(id+"F2.opExtrude","SWEPT_BODY",BODY,{"disambiguationData":[OSD([sQuery(id+"F0.wireOp",EDGE,"E136")])]});
            var Q48;
            Q48=makeQuery(id+"F2.opExtrude","SWEPT_BODY",BODY,{"disambiguationData":[OSD([sQuery(id+"F0.wireOp",EDGE,"E137")])]});
            var Q49;
            Q49=makeQuery(id+"F2.opExtrude","SWEPT_BODY",BODY,{"disambiguationData":[OSD([sQuery(id+"F0.wireOp",EDGE,"E138")])]});
            deleteBodies(context, id + "F4", {"entities" : qUnion([Q0, Q1, Q2, Q3, Q4, Q5, Q6, Q7, Q8, Q9, Q10, Q11, Q12, Q13, Q14, Q15, Q16, Q17, Q18, Q19, Q20, Q21, Q22, Q23, Q24, Q25, Q26, Q27, Q28, Q29, Q30, Q31, Q32, Q33, Q34, Q35, Q36, Q37, Q38, Q39, Q40, Q41, Q42, Q43, Q44, Q45, Q46, Q47, Q48, Q49])});
        }
        {
            var Q0;
            Q0=makeQuery(id+"F1.imprint","IMPRINT",FACE,{"disambiguationData":[TD([[makeQuery(id+"F1.imprint","IMPRINT",EDGE,{"derivedFrom":sQuery(id+"F1.wireOp",EDGE,"E142.bottom")}),1.0]])]});
            extrude(context, id + "F5", {"entities" : qUnion([Q0]), "depth" : 12.7 * mm});
        }
        {
            var Q0;
            Q0=makeQuery(id+"F3.opExtrude","SWEPT_BODY",BODY,{"disambiguationData":[OSD([sQuery(id+"F0.wireOp",EDGE,"E10")])]});
            var Q1;
            Q1=makeQuery(id+"F3.opExtrude","SWEPT_BODY",BODY,{"disambiguationData":[OSD([sQuery(id+"F0.wireOp",EDGE,"E14")])]});
            var Q2;
            Q2=makeQuery(id+"F3.opExtrude","SWEPT_BODY",BODY,{"disambiguationData":[OSD([sQuery(id+"F0.wireOp",EDGE,"E15")])]});
            var Q3;
            Q3=makeQuery(id+"F3.opExtrude","SWEPT_BODY",BODY,{"disambiguationData":[OSD([sQuery(id+"F0.wireOp",EDGE,"E16")])]});
            var Q4;
            Q4=makeQuery(id+"F3.opExtrude","SWEPT_BODY",BODY,{"disambiguationData":[OSD([sQuery(id+"F0.wireOp",EDGE,"E20")])]});
            var Q5;
            Q5=makeQuery(id+"F3.opExtrude","SWEPT_BODY",BODY,{"disambiguationData":[OSD([sQuery(id+"F0.wireOp",EDGE,"E29")])]});
            var Q6;
            Q6=makeQuery(id+"F3.opExtrude","SWEPT_BODY",BODY,{"disambiguationData":[OSD([sQuery(id+"F0.wireOp",EDGE,"E30")])]});
            var Q7;
            Q7=makeQuery(id+"F3.opExtrude","SWEPT_BODY",BODY,{"disambiguationData":[OSD([sQuery(id+"F0.wireOp",EDGE,"E31")])]});
            var Q8;
            Q8=makeQuery(id+"F3.opExtrude","SWEPT_BODY",BODY,{"disambiguationData":[OSD([sQuery(id+"F0.wireOp",EDGE,"E32")])]});
            var Q9;
            Q9=makeQuery(id+"F3.opExtrude","SWEPT_BODY",BODY,{"disambiguationData":[OSD([sQuery(id+"F0.wireOp",EDGE,"E33")])]});
            var Q10;
            Q10=makeQuery(id+"F3.opExtrude","SWEPT_BODY",BODY,{"disambiguationData":[OSD([sQuery(id+"F0.wireOp",EDGE,"E58")])]});
            var Q11;
            Q11=makeQuery(id+"F3.opExtrude","SWEPT_BODY",BODY,{"disambiguationData":[OSD([sQuery(id+"F0.wireOp",EDGE,"E59")])]});
            var Q12;
            Q12=makeQuery(id+"F3.opExtrude","SWEPT_BODY",BODY,{"disambiguationData":[OSD([sQuery(id+"F0.wireOp",EDGE,"E60")])]});
            var Q13;
            Q13=makeQuery(id+"F3.opExtrude","SWEPT_BODY",BODY,{"disambiguationData":[OSD([sQuery(id+"F0.wireOp",EDGE,"E61")])]});
            var Q14;
            Q14=makeQuery(id+"F3.opExtrude","SWEPT_BODY",BODY,{"disambiguationData":[OSD([sQuery(id+"F0.wireOp",EDGE,"E62")])]});
            var Q15;
            Q15=makeQuery(id+"F3.opExtrude","SWEPT_BODY",BODY,{"disambiguationData":[OSD([sQuery(id+"F0.wireOp",EDGE,"E63")])]});
            var Q16;
            Q16=makeQuery(id+"F3.opExtrude","SWEPT_BODY",BODY,{"disambiguationData":[OSD([sQuery(id+"F0.wireOp",EDGE,"E64")])]});
            var Q17;
            Q17=makeQuery(id+"F3.opExtrude","SWEPT_BODY",BODY,{"disambiguationData":[OSD([sQuery(id+"F0.wireOp",EDGE,"E65")])]});
            var Q18;
            Q18=makeQuery(id+"F3.opExtrude","SWEPT_BODY",BODY,{"disambiguationData":[OSD([sQuery(id+"F0.wireOp",EDGE,"E66")])]});
            var Q19;
            Q19=makeQuery(id+"F3.opExtrude","SWEPT_BODY",BODY,{"disambiguationData":[OSD([sQuery(id+"F0.wireOp",EDGE,"E67")])]});
            var Q20;
            Q20=makeQuery(id+"F3.opExtrude","SWEPT_BODY",BODY,{"disambiguationData":[OSD([sQuery(id+"F0.wireOp",EDGE,"E68")])]});
            var Q21;
            Q21=makeQuery(id+"F3.opExtrude","SWEPT_BODY",BODY,{"disambiguationData":[OSD([sQuery(id+"F0.wireOp",EDGE,"E69")])]});
            var Q22;
            Q22=makeQuery(id+"F3.opExtrude","SWEPT_BODY",BODY,{"disambiguationData":[OSD([sQuery(id+"F0.wireOp",EDGE,"E70")])]});
            var Q23;
            Q23=makeQuery(id+"F3.opExtrude","SWEPT_BODY",BODY,{"disambiguationData":[OSD([sQuery(id+"F0.wireOp",EDGE,"E71")])]});
            var Q24;
            Q24=makeQuery(id+"F3.opExtrude","SWEPT_BODY",BODY,{"disambiguationData":[OSD([sQuery(id+"F0.wireOp",EDGE,"E72")])]});
            var Q25;
            Q25=makeQuery(id+"F3.opExtrude","SWEPT_BODY",BODY,{"disambiguationData":[OSD([sQuery(id+"F0.wireOp",EDGE,"E114")])]});
            var Q26;
            Q26=makeQuery(id+"F3.opExtrude","SWEPT_BODY",BODY,{"disambiguationData":[OSD([sQuery(id+"F0.wireOp",EDGE,"E115")])]});
            var Q27;
            Q27=makeQuery(id+"F3.opExtrude","SWEPT_BODY",BODY,{"disambiguationData":[OSD([sQuery(id+"F0.wireOp",EDGE,"E116")])]});
            var Q28;
            Q28=makeQuery(id+"F3.opExtrude","SWEPT_BODY",BODY,{"disambiguationData":[OSD([sQuery(id+"F0.wireOp",EDGE,"E117")])]});
            var Q29;
            Q29=makeQuery(id+"F3.opExtrude","SWEPT_BODY",BODY,{"disambiguationData":[OSD([sQuery(id+"F0.wireOp",EDGE,"E118")])]});
            var Q30;
            Q30=makeQuery(id+"F3.opExtrude","SWEPT_BODY",BODY,{"disambiguationData":[OSD([sQuery(id+"F0.wireOp",EDGE,"E119")])]});
            var Q31;
            Q31=makeQuery(id+"F3.opExtrude","SWEPT_BODY",BODY,{"disambiguationData":[OSD([sQuery(id+"F0.wireOp",EDGE,"E120")])]});
            var Q32;
            Q32=makeQuery(id+"F3.opExtrude","SWEPT_BODY",BODY,{"disambiguationData":[OSD([sQuery(id+"F0.wireOp",EDGE,"E121")])]});
            var Q33;
            Q33=makeQuery(id+"F3.opExtrude","SWEPT_BODY",BODY,{"disambiguationData":[OSD([sQuery(id+"F0.wireOp",EDGE,"E122")])]});
            var Q34;
            Q34=makeQuery(id+"F3.opExtrude","SWEPT_BODY",BODY,{"disambiguationData":[OSD([sQuery(id+"F0.wireOp",EDGE,"E123")])]});
            var Q35;
            Q35=makeQuery(id+"F3.opExtrude","SWEPT_BODY",BODY,{"disambiguationData":[OSD([sQuery(id+"F0.wireOp",EDGE,"E124")])]});
            var Q36;
            Q36=makeQuery(id+"F3.opExtrude","SWEPT_BODY",BODY,{"disambiguationData":[OSD([sQuery(id+"F0.wireOp",EDGE,"E125")])]});
            var Q37;
            Q37=makeQuery(id+"F3.opExtrude","SWEPT_BODY",BODY,{"disambiguationData":[OSD([sQuery(id+"F0.wireOp",EDGE,"E126")])]});
            var Q38;
            Q38=makeQuery(id+"F3.opExtrude","SWEPT_BODY",BODY,{"disambiguationData":[OSD([sQuery(id+"F0.wireOp",EDGE,"E127")])]});
            var Q39;
            Q39=makeQuery(id+"F3.opExtrude","SWEPT_BODY",BODY,{"disambiguationData":[OSD([sQuery(id+"F0.wireOp",EDGE,"E128")])]});
            var Q40;
            Q40=makeQuery(id+"F3.opExtrude","SWEPT_BODY",BODY,{"disambiguationData":[OSD([sQuery(id+"F0.wireOp",EDGE,"E129")])]});
            var Q41;
            Q41=makeQuery(id+"F3.opExtrude","SWEPT_BODY",BODY,{"disambiguationData":[OSD([sQuery(id+"F0.wireOp",EDGE,"E130")])]});
            var Q42;
            Q42=makeQuery(id+"F3.opExtrude","SWEPT_BODY",BODY,{"disambiguationData":[OSD([sQuery(id+"F0.wireOp",EDGE,"E131")])]});
            var Q43;
            Q43=makeQuery(id+"F3.opExtrude","SWEPT_BODY",BODY,{"disambiguationData":[OSD([sQuery(id+"F0.wireOp",EDGE,"E132")])]});
            var Q44;
            Q44=makeQuery(id+"F3.opExtrude","SWEPT_BODY",BODY,{"disambiguationData":[OSD([sQuery(id+"F0.wireOp",EDGE,"E133")])]});
            var Q45;
            Q45=makeQuery(id+"F3.opExtrude","SWEPT_BODY",BODY,{"disambiguationData":[OSD([sQuery(id+"F0.wireOp",EDGE,"E134")])]});
            var Q46;
            Q46=makeQuery(id+"F3.opExtrude","SWEPT_BODY",BODY,{"disambiguationData":[OSD([sQuery(id+"F0.wireOp",EDGE,"E135")])]});
            var Q47;
            Q47=makeQuery(id+"F3.opExtrude","SWEPT_BODY",BODY,{"disambiguationData":[OSD([sQuery(id+"F0.wireOp",EDGE,"E136")])]});
            var Q48;
            Q48=makeQuery(id+"F3.opExtrude","SWEPT_BODY",BODY,{"disambiguationData":[OSD([sQuery(id+"F0.wireOp",EDGE,"E137")])]});
            var Q49;
            Q49=makeQuery(id+"F3.opExtrude","SWEPT_BODY",BODY,{"disambiguationData":[OSD([sQuery(id+"F0.wireOp",EDGE,"E138")])]});
            var Q50;
            Q50=makeQuery(id+"F5.opExtrude","SWEPT_BODY",BODY,{"disambiguationData":[OSD([sQuery(id+"F1.wireOp",EDGE,"E142.bottom"),sQuery(id+"F1.wireOp",EDGE,"E142.left"),sQuery(id+"F1.wireOp",EDGE,"E142.right"),sQuery(id+"F1.wireOp",EDGE,"E143.filletArc"),sQuery(id+"F1.wireOp",EDGE,"E144.filletArc"),sQuery(id+"F1.wireOp",EDGE,"E146"),sQuery(id+"F1.wireOp",EDGE,"E150")])]});
            booleanBodies(context, id + "F6", {"operationType" : BooleanOperationType.SUBTRACTION, "tools" : qUnion([Q0, Q1, Q2, Q3, Q4, Q5, Q6, Q7, Q8, Q9, Q10, Q11, Q12, Q13, Q14, Q15, Q16, Q17, Q18, Q19, Q20, Q21, Q22, Q23, Q24, Q25, Q26, Q27, Q28, Q29, Q30, Q31, Q32, Q33, Q34, Q35, Q36, Q37, Q38, Q39, Q40, Q41, Q42, Q43, Q44, Q45, Q46, Q47, Q48, Q49]), "targets" : qUnion([Q50])});
        }
    });
